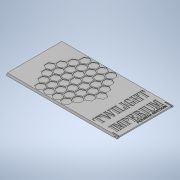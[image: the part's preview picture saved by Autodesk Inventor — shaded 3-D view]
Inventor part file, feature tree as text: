
AUTODESK INVENTOR PART (.ipt)
format: ipt  version: 2021 (Build 250183000, 183)  size: 3,054,080 bytes
history: native  units: mm
features: sketch x4, projected_geometry x4, extrude x3, emboss x1, chamfer x1
ambient origin geometry x8: Origin, YZ Plane, XZ Plane, XY Plane, X Axis, Y Axis, Z Axis, Center Point
bodies: Solid1 (feature_tree)
feature tree (13):
  extrude  "Extrusion1"  Depth=1.5mm
  extrude  "Extrusion2"  Depth=140.85mm TaperAngle=0.0deg
  emboss  "Emboss2"
  extrude  "Extrusion4"  TaperAngle=45.0deg  [1 undecoded]
  chamfer  "Chamfer1"  Distance=0.25mm
  sketch  "Sketch1"  dims[d0=2.0mm d1=1.5mm]
  sketch  "Sketch2"  dims[d2=69.2mm d3=140.85mm d4=0.0mm]
  projected_geometry  "Projected Loop1"
  projected_geometry  "Projected Loop2"
  projected_geometry  "Projected Loop3"
  sketch  "Sketch4"  dims[d5=0.5mm d6=45.0deg]
  projected_geometry  "Projected Loop5"
  sketch  "Sketch6"  dims[d7=0.5mm d8=0.25mm d10=0.6mm d11=60.0deg d12=2.5mm d13=3.0mm d14=0.1mm d15=1.5mm d16=0.8mm d17=8.0mm d18=1.5mm d19=140.85mm d20=0.0mm d25=0.5mm d26=0.0mm d27=25.0mm d28=2.0mm d366=1.2mm d367=1.2mm d368=1.2mm d369=34.0mm d371=1.2mm d372=1.2mm d373=1.2mm d374=60.0mm d376=360.0deg d378=0.0mm d379=0.0mm d380=0.5mm d381=2.0mm d382=45.0deg]
note: 1 required parameter value undecoded (feature->parameter linkage not recoverable at this tier; creation-order binding heuristic only, values carry confidence <= 0.55)
